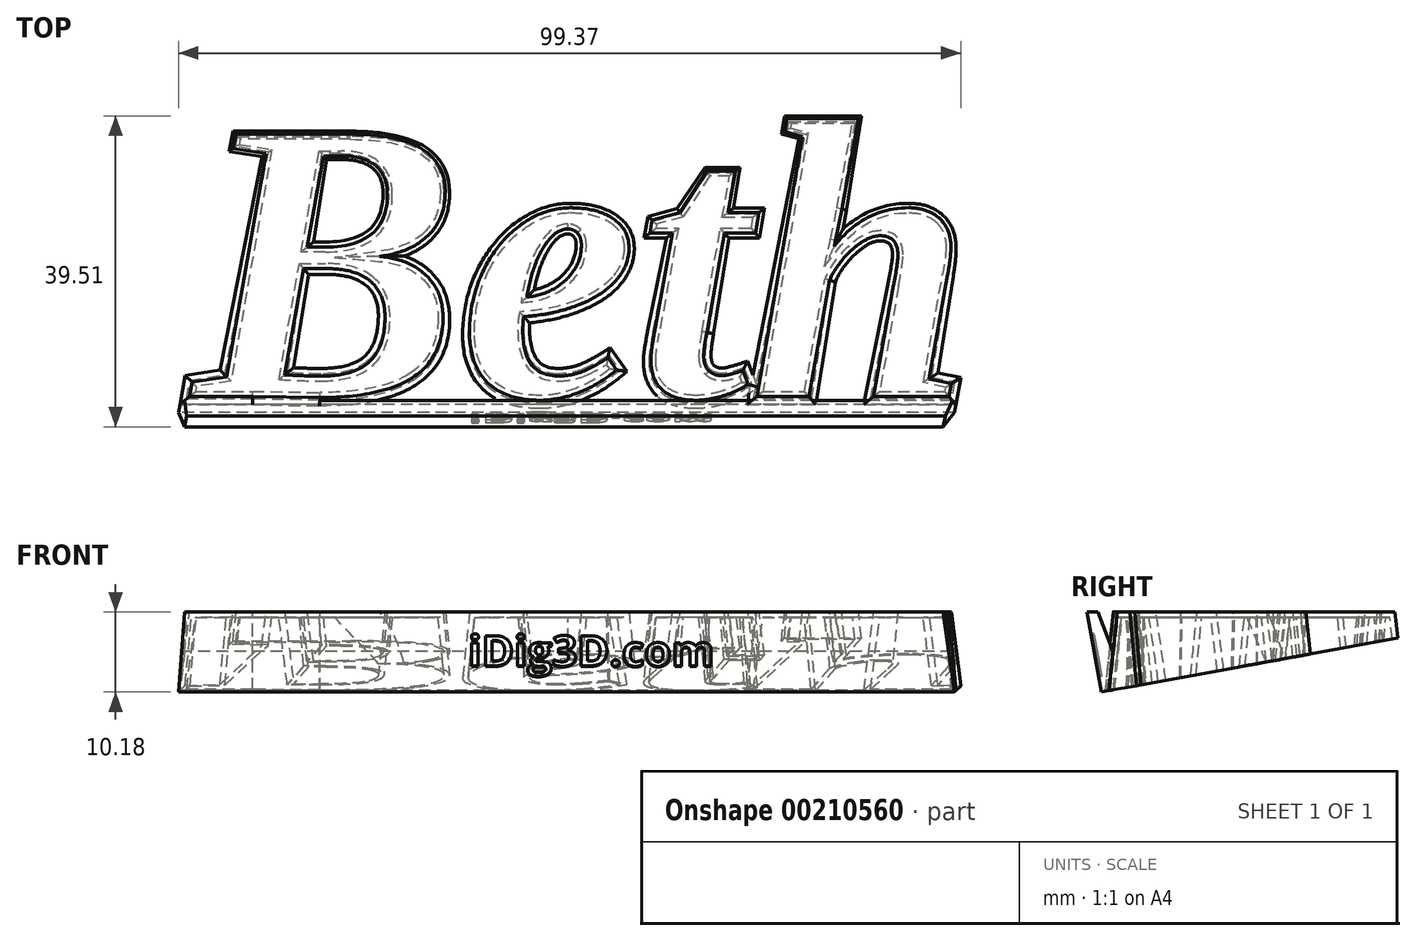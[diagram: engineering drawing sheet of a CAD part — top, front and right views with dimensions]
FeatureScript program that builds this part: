
annotation { "Feature Type Name" : "Feature", "Feature Type Description" : "" }
export const myFeature = defineFeature(function(context is Context, id is Id, definition is map)
    precondition{}
    {
        {
            var Q0;
            Q0=qCreatedBy(makeId("Top.planeOp"),FACE);
            var sketch = newSketch(context, id + "F0", { "sketchPlane" : qUnion([Q0])});
            skText(sketch, "E0", { "text": "Beth", "fontName": "Tinos-BoldItalic.ttf"});
            const initialGuessF0  = {"E0": [-0.05054, -0.01899, 1, 0, 0.0366]};
            skSetInitialGuess(sketch, initialGuessF0);
            skSolve(sketch);
        }
        {
            var Q0;
            Q0=qSketchRegion(id+"F0",true);
            extrude(context, id + "F1", {"entities" : qUnion([Q0]), "oppositeDirection" : true, "depth" : 10 * mm, "hasDraft" : true, "draftAngle" : 6 * degree});
        }
        {
            var Q0;
            Q0=makeQuery(id+"F1.opExtrude","CAP_FACE",FACE,{"disambiguationData":[OSD([sQuery(id+"F0.wireOp",EDGE,"E0.sketch_text.stroke-0"),sQuery(id+"F0.wireOp",EDGE,"E0.sketch_text.stroke-1"),sQuery(id+"F0.wireOp",EDGE,"E0.sketch_text.stroke-2"),sQuery(id+"F0.wireOp",EDGE,"E0.sketch_text.stroke-3"),sQuery(id+"F0.wireOp",EDGE,"E0.sketch_text.stroke-4"),sQuery(id+"F0.wireOp",EDGE,"E0.sketch_text.stroke-5"),sQuery(id+"F0.wireOp",EDGE,"E0.sketch_text.stroke-6"),sQuery(id+"F0.wireOp",EDGE,"E0.sketch_text.stroke-7"),sQuery(id+"F0.wireOp",EDGE,"E0.sketch_text.stroke-8"),sQuery(id+"F0.wireOp",EDGE,"E0.sketch_text.stroke-9"),sQuery(id+"F0.wireOp",EDGE,"E0.sketch_text.stroke-10"),sQuery(id+"F0.wireOp",EDGE,"E0.sketch_text.stroke-11"),sQuery(id+"F0.wireOp",EDGE,"E0.sketch_text.stroke-12"),sQuery(id+"F0.wireOp",EDGE,"E0.sketch_text.stroke-13"),sQuery(id+"F0.wireOp",EDGE,"E0.sketch_text.stroke-14"),sQuery(id+"F0.wireOp",EDGE,"E0.sketch_text.stroke-15"),sQuery(id+"F0.wireOp",EDGE,"E0.sketch_text.stroke-16"),sQuery(id+"F0.wireOp",EDGE,"E0.sketch_text.stroke-17"),sQuery(id+"F0.wireOp",EDGE,"E0.sketch_text.stroke-18"),sQuery(id+"F0.wireOp",EDGE,"E0.sketch_text.stroke-19"),sQuery(id+"F0.wireOp",EDGE,"E0.sketch_text.stroke-20"),sQuery(id+"F0.wireOp",EDGE,"E0.sketch_text.stroke-21"),sQuery(id+"F0.wireOp",EDGE,"E0.sketch_text.stroke-22"),sQuery(id+"F0.wireOp",EDGE,"E0.sketch_text.stroke-23"),sQuery(id+"F0.wireOp",EDGE,"E0.sketch_text.stroke-24"),sQuery(id+"F0.wireOp",EDGE,"E0.sketch_text.stroke-25"),sQuery(id+"F0.wireOp",EDGE,"E0.sketch_text.stroke-26"),sQuery(id+"F0.wireOp",EDGE,"E0.sketch_text.stroke-27")])],"isStart":false});
            var Q1;
            Q1=makeQuery(id+"FcNgDYY6Mbh8Th6_4.opBoolean","MERGE",FACE,{"derivedFrom":[makeQuery(id+"F1.opExtrude","CAP_FACE",FACE,{"disambiguationData":[OSD([sQuery(id+"F0.wireOp",EDGE,"E0.sketch_text.stroke-28"),sQuery(id+"F0.wireOp",EDGE,"E0.sketch_text.stroke-29"),sQuery(id+"F0.wireOp",EDGE,"E0.sketch_text.stroke-30"),sQuery(id+"F0.wireOp",EDGE,"E0.sketch_text.stroke-31"),sQuery(id+"F0.wireOp",EDGE,"E0.sketch_text.stroke-32"),sQuery(id+"F0.wireOp",EDGE,"E0.sketch_text.stroke-33"),sQuery(id+"F0.wireOp",EDGE,"E0.sketch_text.stroke-34"),sQuery(id+"F0.wireOp",EDGE,"E0.sketch_text.stroke-35"),sQuery(id+"F0.wireOp",EDGE,"E0.sketch_text.stroke-36"),sQuery(id+"F0.wireOp",EDGE,"E0.sketch_text.stroke-37"),sQuery(id+"F0.wireOp",EDGE,"E0.sketch_text.stroke-38"),sQuery(id+"F0.wireOp",EDGE,"E0.sketch_text.stroke-39"),sQuery(id+"F0.wireOp",EDGE,"E0.sketch_text.stroke-40"),sQuery(id+"F0.wireOp",EDGE,"E0.sketch_text.stroke-41"),sQuery(id+"F0.wireOp",EDGE,"E0.sketch_text.stroke-42"),sQuery(id+"F0.wireOp",EDGE,"E0.sketch_text.stroke-43"),sQuery(id+"F0.wireOp",EDGE,"E0.sketch_text.stroke-44"),sQuery(id+"F0.wireOp",EDGE,"E0.sketch_text.stroke-45"),sQuery(id+"F0.wireOp",EDGE,"E0.sketch_text.stroke-46"),sQuery(id+"F0.wireOp",EDGE,"E0.sketch_text.stroke-47"),sQuery(id+"F0.wireOp",EDGE,"E0.sketch_text.stroke-48"),sQuery(id+"F0.wireOp",EDGE,"E0.sketch_text.stroke-49"),sQuery(id+"F0.wireOp",EDGE,"E0.sketch_text.stroke-50")])],"isStart":false}),makeQuery(id+"F1.opExtrude","CAP_FACE",FACE,{"disambiguationData":[OSD([sQuery(id+"F0.wireOp",EDGE,"E0.sketch_text.stroke-51"),sQuery(id+"F0.wireOp",EDGE,"E0.sketch_text.stroke-52"),sQuery(id+"F0.wireOp",EDGE,"E0.sketch_text.stroke-53"),sQuery(id+"F0.wireOp",EDGE,"E0.sketch_text.stroke-54"),sQuery(id+"F0.wireOp",EDGE,"E0.sketch_text.stroke-55"),sQuery(id+"F0.wireOp",EDGE,"E0.sketch_text.stroke-56"),sQuery(id+"F0.wireOp",EDGE,"E0.sketch_text.stroke-57"),sQuery(id+"F0.wireOp",EDGE,"E0.sketch_text.stroke-58"),sQuery(id+"F0.wireOp",EDGE,"E0.sketch_text.stroke-59"),sQuery(id+"F0.wireOp",EDGE,"E0.sketch_text.stroke-60"),sQuery(id+"F0.wireOp",EDGE,"E0.sketch_text.stroke-61"),sQuery(id+"F0.wireOp",EDGE,"E0.sketch_text.stroke-62"),sQuery(id+"F0.wireOp",EDGE,"E0.sketch_text.stroke-63"),sQuery(id+"F0.wireOp",EDGE,"E0.sketch_text.stroke-64"),sQuery(id+"F0.wireOp",EDGE,"E0.sketch_text.stroke-65"),sQuery(id+"F0.wireOp",EDGE,"E0.sketch_text.stroke-66"),sQuery(id+"F0.wireOp",EDGE,"E0.sketch_text.stroke-67"),sQuery(id+"F0.wireOp",EDGE,"E0.sketch_text.stroke-68"),sQuery(id+"F0.wireOp",EDGE,"E0.sketch_text.stroke-69"),sQuery(id+"F0.wireOp",EDGE,"E0.sketch_text.stroke-70"),sQuery(id+"F0.wireOp",EDGE,"E0.sketch_text.stroke-71")])],"isStart":false}),makeQuery(id+"F1.opExtrude","CAP_FACE",FACE,{"disambiguationData":[OSD([sQuery(id+"F0.wireOp",EDGE,"E0.sketch_text.stroke-72"),sQuery(id+"F0.wireOp",EDGE,"E0.sketch_text.stroke-73"),sQuery(id+"F0.wireOp",EDGE,"E0.sketch_text.stroke-74"),sQuery(id+"F0.wireOp",EDGE,"E0.sketch_text.stroke-75"),sQuery(id+"F0.wireOp",EDGE,"E0.sketch_text.stroke-76"),sQuery(id+"F0.wireOp",EDGE,"E0.sketch_text.stroke-77"),sQuery(id+"F0.wireOp",EDGE,"E0.sketch_text.stroke-78"),sQuery(id+"F0.wireOp",EDGE,"E0.sketch_text.stroke-79"),sQuery(id+"F0.wireOp",EDGE,"E0.sketch_text.stroke-80"),sQuery(id+"F0.wireOp",EDGE,"E0.sketch_text.stroke-81"),sQuery(id+"F0.wireOp",EDGE,"E0.sketch_text.stroke-82"),sQuery(id+"F0.wireOp",EDGE,"E0.sketch_text.stroke-83"),sQuery(id+"F0.wireOp",EDGE,"E0.sketch_text.stroke-84"),sQuery(id+"F0.wireOp",EDGE,"E0.sketch_text.stroke-85"),sQuery(id+"F0.wireOp",EDGE,"E0.sketch_text.stroke-86"),sQuery(id+"F0.wireOp",EDGE,"E0.sketch_text.stroke-87"),sQuery(id+"F0.wireOp",EDGE,"E0.sketch_text.stroke-88"),sQuery(id+"F0.wireOp",EDGE,"E0.sketch_text.stroke-89"),sQuery(id+"F0.wireOp",EDGE,"E0.sketch_text.stroke-90"),sQuery(id+"F0.wireOp",EDGE,"E0.sketch_text.stroke-91"),sQuery(id+"F0.wireOp",EDGE,"E0.sketch_text.stroke-92"),sQuery(id+"F0.wireOp",EDGE,"E0.sketch_text.stroke-93")])],"isStart":false})]});
            shell(context, id + "F2", {"entities" : qUnion([Q0, Q1]), "thickness" : .7 * mm});
        }
        {
            var Q0;
            Q0=qCreatedBy(makeId("Right.planeOp"),FACE);
            var sketch = newSketch(context, id + "F3", { "sketchPlane" : qUnion([Q0])});
            skLineSegment(sketch, "E1.1", {"start": v(-20.04, -10) * mm, "end": v(-18.99, 0) * mm});
            skLineSegment(sketch, "E2", {"start": v(-22.87, 0) * mm, "end": v(-21.02, -10.18) * mm});
            skLineSegment(sketch, "E3", {"start": v(-21.02, -10.18) * mm, "end": v(16.64, -3.33) * mm});
            skLineSegment(sketch, "E4.0", {"start": v(17.34, -10) * mm, "end": v(17, -6.67) * mm});
            skLineSegment(sketch, "E5", {"start": v(-19.51, -5) * mm, "end": v(-20.04, -10) * mm});
            skLineSegment(sketch, "E6", {"start": v(-21.02, -10) * mm, "end": v(-21.02, -10.18) * mm});
            skLineSegment(sketch, "E7", {"start": v(-21.02, -10) * mm, "end": v(17.34, -10) * mm});
            skLineSegment(sketch, "E8", {"start": v(16.64, -3.33) * mm, "end": v(16.3, 0) * mm});
            skLineSegment(sketch, "E9", {"start": v(17, -6.67) * mm, "end": v(16.64, -3.33) * mm});
            skPoint(sketch, "E10.orphan", {"position": v(17.34, -10) * mm});
            skLineSegment(sketch, "E11", {"start": v(-22.87, 0) * mm, "end": v(-21.47, 0) * mm});
            skLineSegment(sketch, "E12", {"start": v(-21.47, 0) * mm, "end": v(-19.51, -5) * mm});
            skSolve(sketch);
        }
        {
            var Q0;
            {var subQ4=sQuery(id+"F3.wireOp",EDGE,"E4.0");Q0=makeQuery(id+"F3.imprint","IMPRINT",FACE,{"disambiguationData":[TD([[makeQuery(id+"F3.imprint","IMPRINT",EDGE,{"derivedFrom":subQ4}),1.0]])]});}
            var Q1;
            Q1=makeQuery(id+"F1.opExtrude","SWEPT_FACE",FACE,{"disambiguationData":[OSD([sQuery(id+"F0.wireOp",EDGE,"E0.sketch_text.stroke-78")])]});
            var Q2;
            Q2=makeQuery(id+"F1.opExtrude","SWEPT_FACE",FACE,{"disambiguationData":[OSD([sQuery(id+"F0.wireOp",EDGE,"E0.sketch_text.stroke-15")])]});
            extrude(context, id + "F4", {"entities" : qUnion([Q0]), "operationType" : NewBodyOperationType.REMOVE, "endBound" : BoundingType.UP_TO_SURFACE, "endBoundEntityFace" : qUnion([Q1]), "depth" : 25 * mm, "hasSecondDirection" : true, "secondDirectionBound" : SecondDirectionBoundingType.UP_TO_SURFACE, "secondDirectionOppositeDirection" : true, "secondDirectionBoundEntityFace" : qUnion([Q2]), "secondDirectionDepth" : 25 * mm});
        }
        {
            var Q0;
            {var subQ4=sQuery(id+"F3.wireOp",EDGE,"E2");Q0=makeQuery(id+"F3.imprint","IMPRINT",FACE,{"disambiguationData":[TD([[makeQuery(id+"F3.imprint","IMPRINT",EDGE,{"derivedFrom":subQ4}),1.0]])]});}
            var Q1;
            {var subQ0=sQuery(id+"F3.wireOp",EDGE,"E6");Q1=makeQuery(id+"F3.imprint","IMPRINT",FACE,{"disambiguationData":[TD([[makeQuery(id+"F3.imprint","IMPRINT",EDGE,{"derivedFrom":subQ0}),1.0]])]});}
            var Q2;
            Q2=makeQuery(id+"F1.opExtrude","SWEPT_FACE",FACE,{"disambiguationData":[OSD([sQuery(id+"F0.wireOp",EDGE,"E0.sketch_text.stroke-78")])]});
            var Q3;
            Q3=makeQuery(id+"F1.opExtrude","SWEPT_FACE",FACE,{"disambiguationData":[OSD([sQuery(id+"F0.wireOp",EDGE,"E0.sketch_text.stroke-15")])]});
            extrude(context, id + "F5", {"entities" : qUnion([Q0, Q1]), "endBound" : BoundingType.UP_TO_SURFACE, "endBoundEntityFace" : qUnion([Q2]), "depth" : 25 * mm, "hasSecondDirection" : true, "secondDirectionBound" : SecondDirectionBoundingType.UP_TO_SURFACE, "secondDirectionOppositeDirection" : true, "secondDirectionBoundEntityFace" : qUnion([Q3]), "secondDirectionDepth" : 25 * mm});
        }
        {
            var Q0;
            Q0=makeQuery(id+"F5.opExtrude","SWEPT_FACE",FACE,{"disambiguationData":[OSD([sQuery(id+"F3.wireOp",EDGE,"E2")])]});
            var sketch = newSketch(context, id + "F6", { "sketchPlane" : qUnion([Q0])});
            skText(sketch, "E13", { "text": "iDig3D.com", "fontName": "OpenSans-Bold.ttf"});
            const initialGuessF6  = {"E13": [-0.0156, -0.00296, 1, 0, 0.004]};
            skSetInitialGuess(sketch, initialGuessF6);
            skSolve(sketch);
        }
        {
            var Q0;
            Q0=qSketchRegion(id+"F6",true);
            extrude(context, id + "F7", {"entities" : qUnion([Q0]), "operationType" : NewBodyOperationType.REMOVE, "oppositeDirection" : true, "depth" : .4 * mm});
        }
    });
